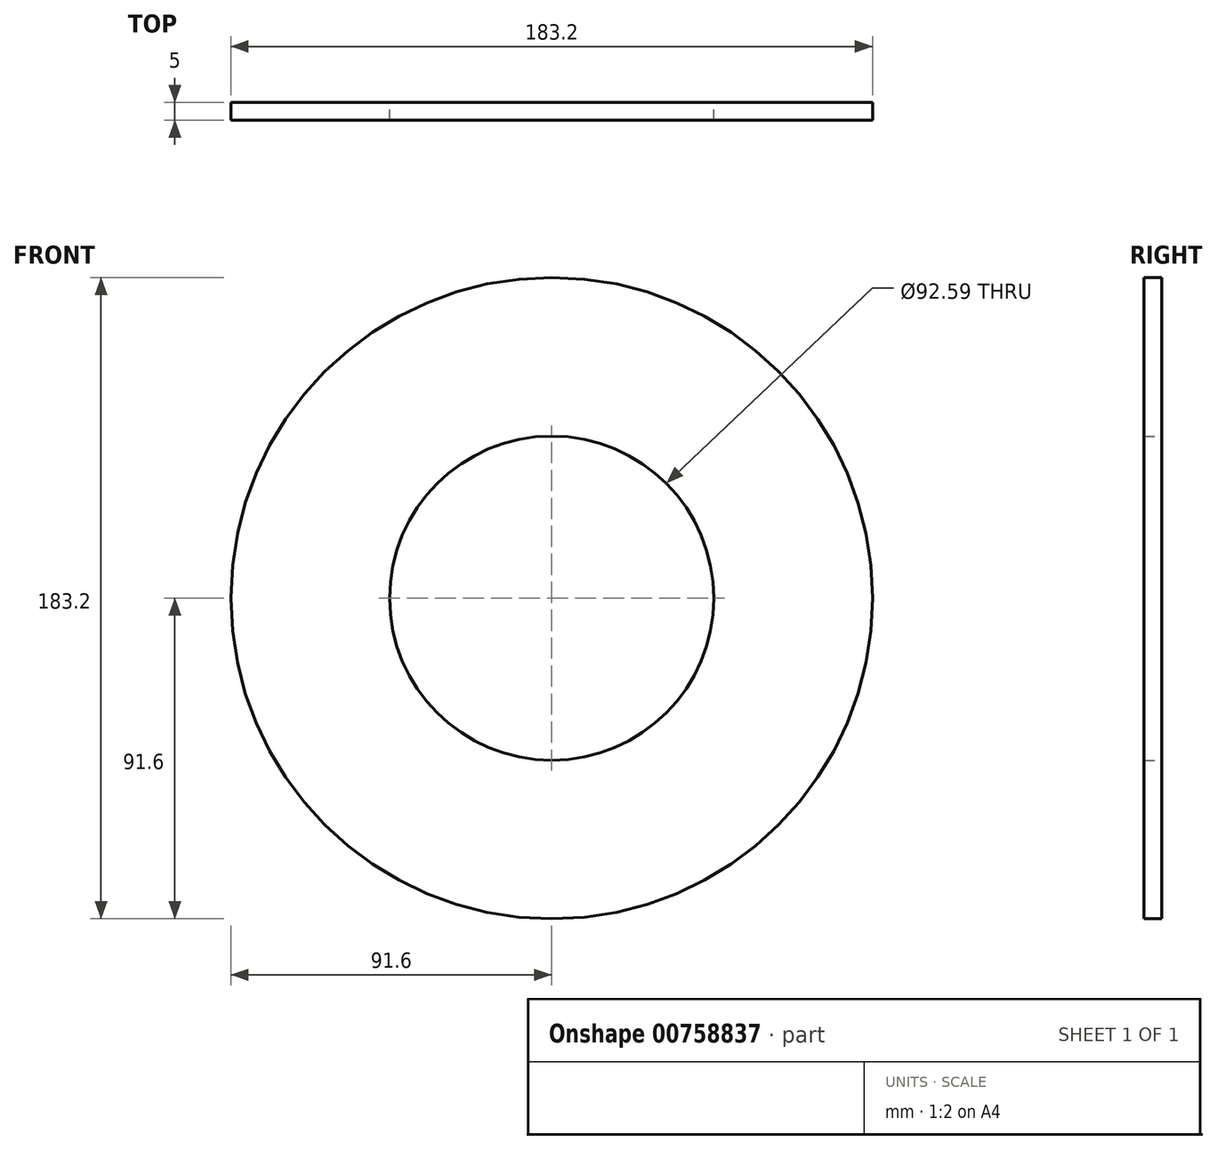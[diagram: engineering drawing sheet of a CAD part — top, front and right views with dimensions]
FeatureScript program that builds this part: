
annotation { "Feature Type Name" : "Feature", "Feature Type Description" : "" }
export const myFeature = defineFeature(function(context is Context, id is Id, definition is map)
    precondition{}
    {
        {
            var Q0;
            Q0=qCreatedBy(makeId("Front.planeOp"),FACE);
            var sketch = newSketch(context, id + "F0", { "sketchPlane" : qUnion([Q0])});
            skCircle(sketch, "E0", {"center": v(0, 0) * mm, "radius": 57.31 * mm});
            skCircle(sketch, "E1", {"center": v(0, 0) * mm, "radius": 46.3 * mm});
            skCircle(sketch, "E2", {"center": v(0, 0) * mm, "radius": 91.6 * mm});
            skSolve(sketch);
        }
        {
            var Q0;
            Q0=makeQuery(id+"F0.imprint","IMPRINT",FACE,{"disambiguationData":[TD([[makeQuery(id+"F0.imprint","IMPRINT",EDGE,{"derivedFrom":sQuery(id+"F0.wireOp",EDGE,"E0")}),-1.0]])]});
            var Q1;
            Q1=makeQuery(id+"F0.imprint","IMPRINT",FACE,{"disambiguationData":[TD([[makeQuery(id+"F0.imprint","IMPRINT",EDGE,{"derivedFrom":sQuery(id+"F0.wireOp",EDGE,"E0")}),1.0]])]});
            extrude(context, id + "F1", {"entities" : qUnion([Q0, Q1]), "depth" : 5 * mm, "offsetDistance" : 25 * mm});
        }
        {
            var Q0;
            Q0=qCreatedBy(makeId("Front.planeOp"),FACE);
            var sketch = newSketch(context, id + "F2", { "sketchPlane" : qUnion([Q0])});
            skCircle(sketch, "E3", {"center": v(0, 0) * mm, "radius": 62.7 * mm});
            skSolve(sketch);
        }
        {
            var Q0;
            Q0=sQuery(id+"F2.wireOp",EDGE,"E3");
            extrude(context, id + "F3", {"bodyType" : ToolBodyType.SURFACE, "surfaceEntities" : qUnion([Q0]), "oppositeDirection" : true, "depth" : 25 * mm, "offsetDistance" : 25 * mm});
        }
    });
